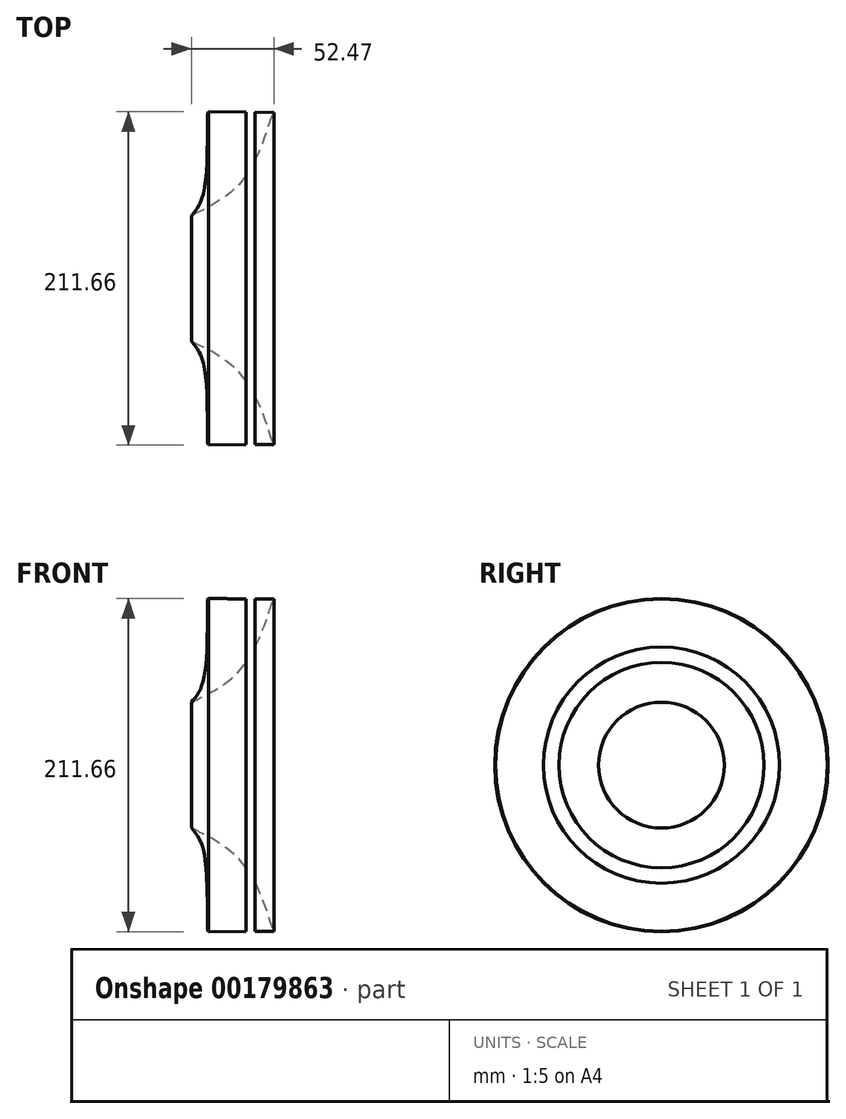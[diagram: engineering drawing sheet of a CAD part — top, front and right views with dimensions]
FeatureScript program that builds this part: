
annotation { "Feature Type Name" : "Feature", "Feature Type Description" : "" }
export const myFeature = defineFeature(function(context is Context, id is Id, definition is map)
    precondition{}
    {
        {
            var Q0;
            Q0=qCreatedBy(makeId("Front.planeOp"),FACE);
            var sketch = newSketch(context, id + "F0", { "sketchPlane" : qUnion([Q0])});
            skLineSegment(sketch, "E0", {"start": v(0, 0) * mm, "end": v(75.8, 0) * mm, "construction": true});
            skLineSegment(sketch, "E1", {"start": v(0, 0) * mm, "end": v(0, 79.93) * mm, "construction": true});
            skFitSpline(sketch, "E2", {"points": [v(0, 39.97) * mm, v(8.18, 56.3) * mm, v(10.43, 104.7) * mm, v(10.8, 105.83) * mm], "startDerivative": vector(27.93, 31.67) * mm, "endDerivative": vector(4.74, 6.1) * mm});
            skFitSpline(sketch, "E3", {"points": [v(0, 39.97) * mm, v(35.95, 66.8) * mm, v(51.72, 104.33) * mm, v(52.47, 105.45) * mm], "startDerivative": vector(85.09, 40.97) * mm, "endDerivative": vector(7.82, 7.2) * mm});
            skLineSegment(sketch, "E4", {"start": v(10.8, 105.83) * mm, "end": v(52.47, 105.45) * mm});
            skLineSegment(sketch, "E5", {"start": v(34.84, 105.61) * mm, "end": v(34.84, 65.18) * mm});
            skLineSegment(sketch, "E6", {"start": v(40.6, 105.56) * mm, "end": v(40.6, 74.97) * mm});
            skSolve(sketch);
        }
        {
            var Q0;
            Q0=makeQuery(id+"F0.imprint","IMPRINT",FACE,{"disambiguationData":[TD([[makeQuery(id+"F0.imprint","IMPRINT",EDGE,{"derivedFrom":sQuery(id+"F0.wireOp",EDGE,"E2")}),-1.0]])]});
            var Q1;
            {var subQ3=sQuery(id+"F0.wireOp",EDGE,"E6");Q1=makeQuery(id+"F0.imprint","IMPRINT",FACE,{"disambiguationData":[TD([[makeQuery(id+"F0.imprint","IMPRINT",EDGE,{"derivedFrom":subQ3}),1.0]])]});}
            var Q2;
            Q2=sQuery(id+"F0.wireOp",EDGE,"E0");
            revolve(context, id + "F1", {"entities" : qUnion([Q0, Q1]), "axis" : qUnion([Q2]), "revolveType" : RevolveType.FULL});
        }
    });
